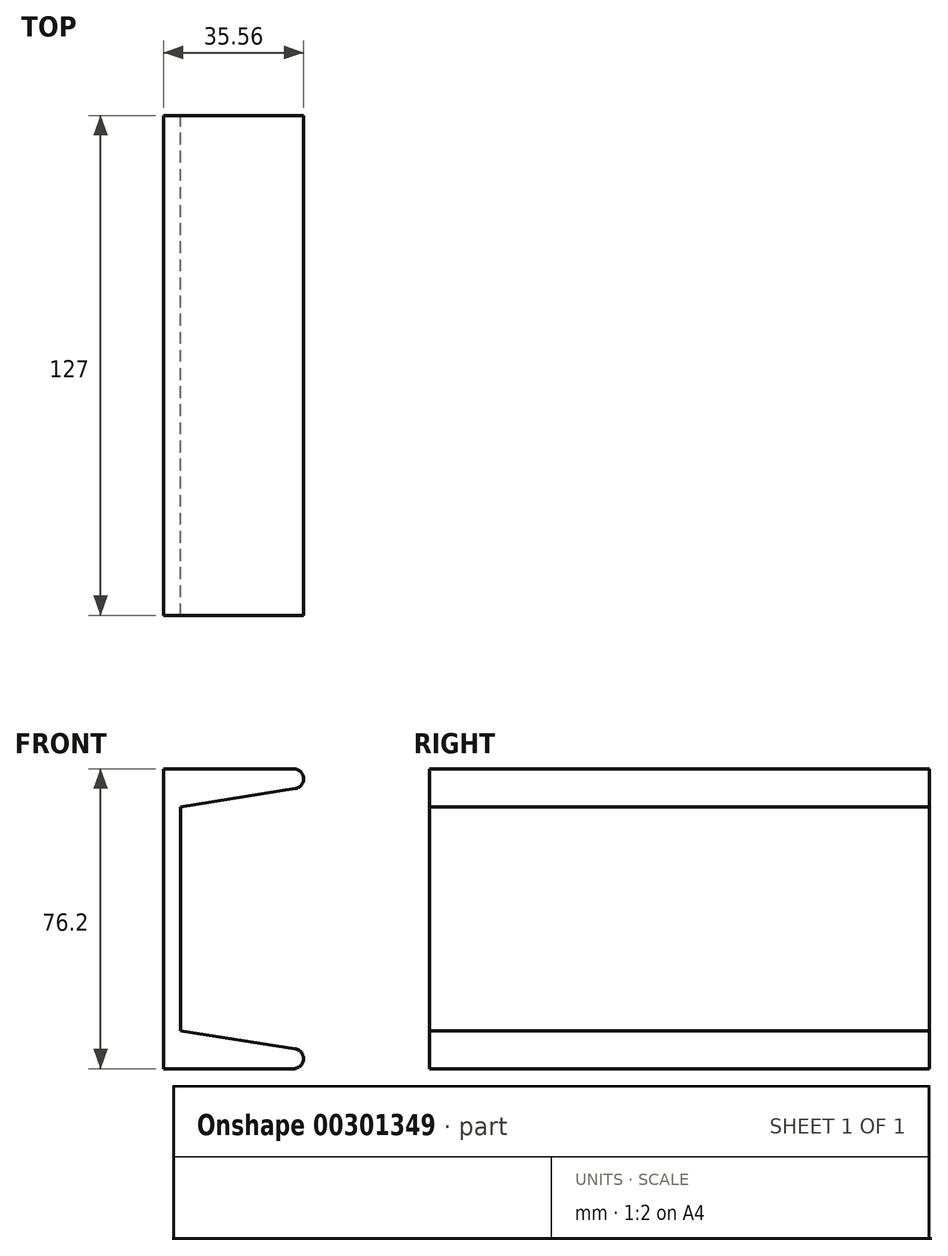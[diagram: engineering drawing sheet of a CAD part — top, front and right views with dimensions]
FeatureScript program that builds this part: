
annotation { "Feature Type Name" : "Feature", "Feature Type Description" : "" }
export const myFeature = defineFeature(function(context is Context, id is Id, definition is map)
    precondition{}
    {
        {
            var Q0;
            Q0=qCreatedBy(makeId("Front.planeOp"),FACE);
            var sketch = newSketch(context, id + "F0", { "sketchPlane" : qUnion([Q0])});
            skLineSegment(sketch, "E0", {"start": v(0, 0) * mm, "end": v(33.02, 0) * mm});
            skLineSegment(sketch, "E1", {"start": v(4.32, 9.66) * mm, "end": v(4.32, 66.54) * mm});
            skLineSegment(sketch, "E2", {"start": v(33.02, 76.2) * mm, "end": v(0, 76.2) * mm});
            skLineSegment(sketch, "E3", {"start": v(0, 76.2) * mm, "end": v(0, 0) * mm});
            skLineSegment(sketch, "E4", {"start": v(4.32, 66.54) * mm, "end": v(33.42, 71.15) * mm});
            skArc(sketch, "E5.filletArc", {"start": v(33.42, 71.15) * mm, "mid": v(35.55, 73.86) * mm, "end": v(33.02, 76.2) * mm});
            skLineSegment(sketch, "E6", {"start": v(4.32, 9.66) * mm, "end": v(33.42, 5.05) * mm});
            skArc(sketch, "E7.filletArc", {"start": v(33.02, 0) * mm, "mid": v(35.55, 2.34) * mm, "end": v(33.42, 5.05) * mm});
            skSolve(sketch);
        }
        {
            var Q0;
            Q0=makeQuery(id+"F0.imprint","IMPRINT",FACE,{"disambiguationData":[TD([[makeQuery(id+"F0.imprint","IMPRINT",EDGE,{"derivedFrom":sQuery(id+"F0.wireOp",EDGE,"E0")}),1.0]])]});
            extrude(context, id + "F1", {"entities" : qUnion([Q0]), "depth" : 127 * mm});
        }
    });
